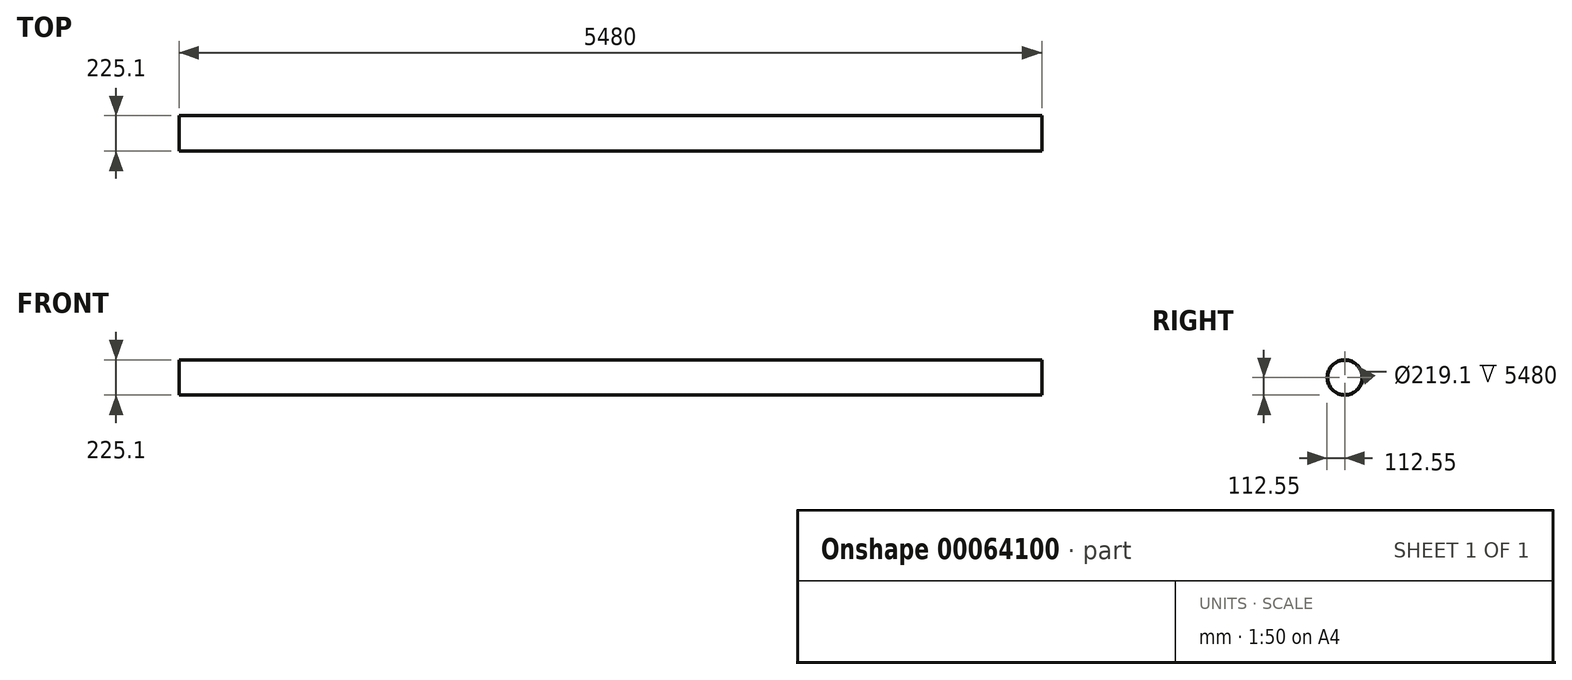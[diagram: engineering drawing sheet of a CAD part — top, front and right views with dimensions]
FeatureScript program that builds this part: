
annotation { "Feature Type Name" : "Feature", "Feature Type Description" : "" }
export const myFeature = defineFeature(function(context is Context, id is Id, definition is map)
    precondition{}
    {
        {
            var Q0;
            Q0=qCreatedBy(makeId("Right.planeOp"),FACE);
            var sketch = newSketch(context, id + "F0", { "sketchPlane" : qUnion([Q0])});
            skCircle(sketch, "E0", {"center": v(0, 0) * mm, "radius": 109.55 * mm});
            skCircle(sketch, "E1", {"center": v(0, 0) * mm, "radius": 112.55 * mm});
            skSolve(sketch);
        }
        {
            var Q0;
            Q0=makeQuery(id+"F0.imprint","IMPRINT",FACE,{"disambiguationData":[TD([[makeQuery(id+"F0.imprint","IMPRINT",EDGE,{"derivedFrom":sQuery(id+"F0.wireOp",EDGE,"E0")}),-1.0]])]});
            extrude(context, id + "F1", {"entities" : qUnion([Q0]), "depth" : 5480 * mm});
        }
    });
